# Revit family: Maxlogic déclancheur Manuel Adressable
name_source: partatom
category: Fire Alarm Devices
units: mm (PartAtom-declared; Revit-internal decimal feet)

## family parameters
Cut with Voids When Loaded = No
Host = Face
Maintain Annotation Orientation = Yes
OmniClass Number = 23.85.30.21
OmniClass Title = Environmental Detection/Registration
Part Type = Normal
Room Calculation Point = No
Round Connector Dimension = Use Diameter
Shared = No

## types (2) — shared parameters
Adresse ligne 1 = Şerifali Mahallesi Kutup Sokak No:27/1-2-4 Ümraniye TR-34775 İSTANBUL
Charger adresse d'appareil = Appareil d'adressage à Main
Code de  Performance = EN 54-11 ve EN 54-17
Couleur = Rouge
Couvercle de protection = PS200
Deuxime Matèriel = Plastique
Durée de la garantie Travail = 2
Durée de la garantie réservé = 2
Hauteur Nominale = 97,5 mm
Largeur Nominale = 71 mm
Longeur Nominale = 93 mm
Manuel d'installation = https://mavilielektronik.com
Manufacturer = Mavili Elektronik Ticaret A.Ş.
Matériel Principe = Plastique Rouge PC/ABS
Model = MaxLogic
Numèro de Fax = (+)90 216 466 45 10
Poids = 270 g
Surface de Montage = Montage à Mur
Tempèrature de Fonctionnement = (-30°C) - (+70°C)
URL = https://www.mavili.com.tr
Unité de durée de garantie = Ans
Voltage de fonctionnement (default) = 24 V/DC
protection de Classe = IP67
voltage fonction d'opération = 18-33V/DC
zero-valued in all types: Cost, Default Elevation

## per-type parameters (varying)
| type | Code de Produit | Description | Hauteur de Montage |
| Maxlogic Adressable Déclancheur Manuel réarmable Etanche IP67 | ML-1730 | Adressable Déclancheur Manuel réarmable Etanche IP67 | Hauteur 1.4m du sol (+/- 200mm) |
| Maxlogic Adressable Déclancheur Manuel réarmable Etanche IP67,Isolateur de Court-Circuit | ML-1730.SCI | Adressable Déclancheur Manuel réarmable Etanche IP67,Isolateur de Court-Circuit | Hauteur  1.4m du Sol (+/- 200mm) |

## geometry (parser evidence)
native form markers: Sweep x2
no freeform markers — native parametric forms only
